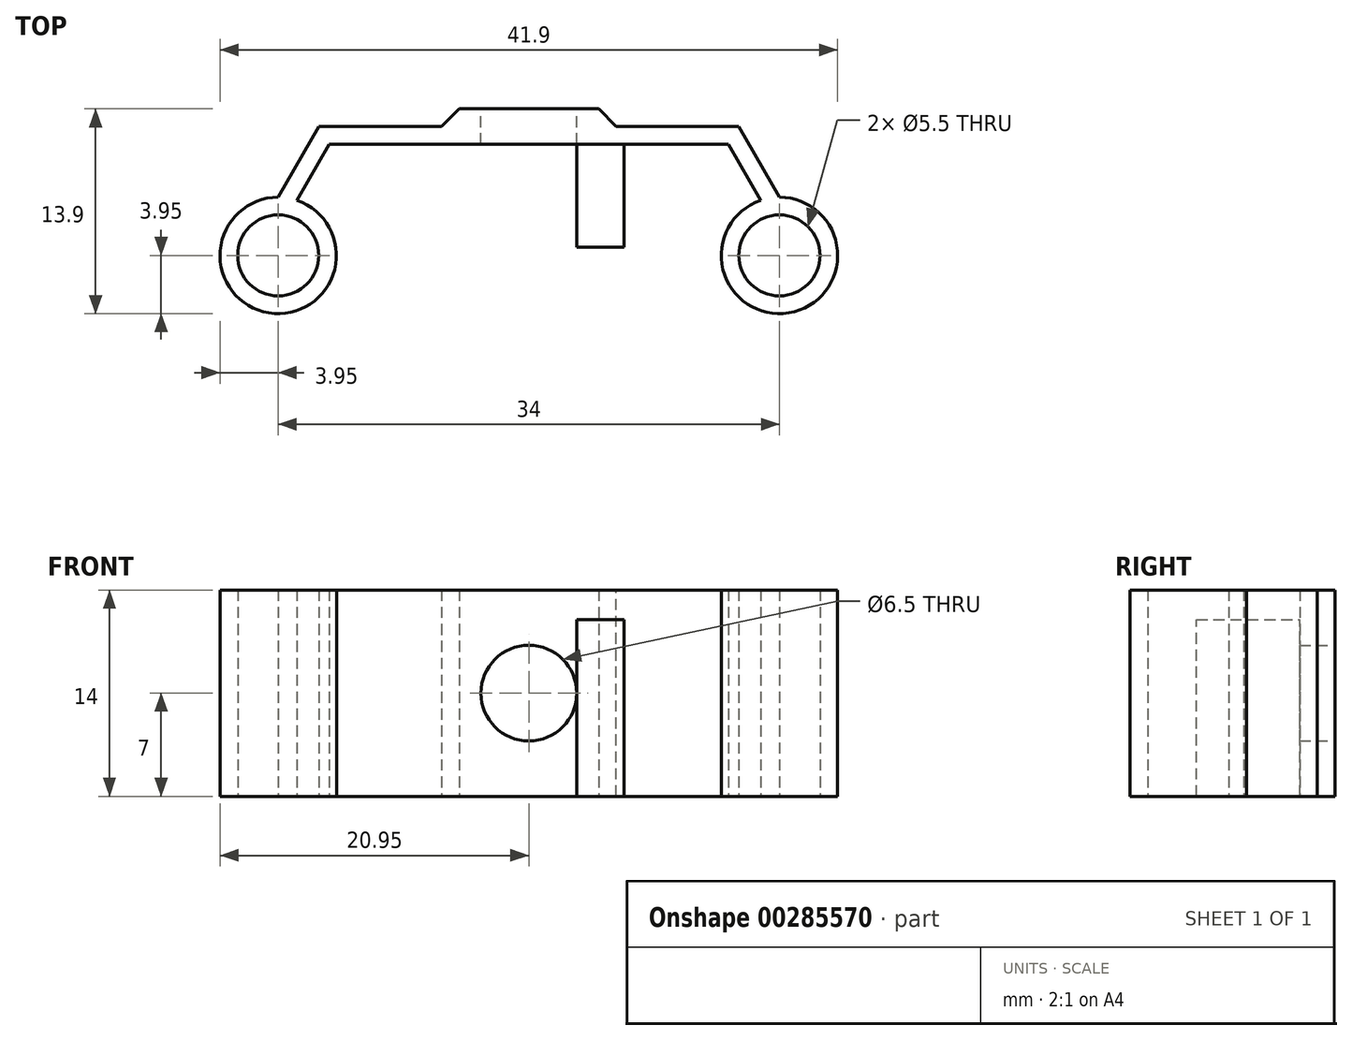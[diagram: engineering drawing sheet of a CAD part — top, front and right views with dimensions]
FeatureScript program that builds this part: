
annotation { "Feature Type Name" : "Feature", "Feature Type Description" : "" }
export const myFeature = defineFeature(function(context is Context, id is Id, definition is map)
    precondition{}
    {
        {
            var Q0;
            Q0=qCreatedBy(makeId("Top.planeOp"),FACE);
            var sketch = newSketch(context, id + "F0", { "sketchPlane" : qUnion([Q0])});
            skCircle(sketch, "E0", {"center": v(0, 0) * mm, "radius": 2.75 * mm});
            skCircle(sketch, "E1.0", {"center": v(0, 0) * mm, "radius": 3.95 * mm});
            skCircle(sketch, "E2", {"center": v(34, 0) * mm, "radius": 2.75 * mm});
            skCircle(sketch, "E3.0", {"center": v(34, 0) * mm, "radius": 3.95 * mm});
            skLineSegment(sketch, "E4", {"start": v(0, 3.95) * mm, "end": v(2.77, 8.75) * mm});
            skLineSegment(sketch, "E5", {"start": v(2.77, 8.75) * mm, "end": v(31.23, 8.75) * mm});
            skLineSegment(sketch, "E6", {"start": v(31.23, 8.75) * mm, "end": v(34, 3.95) * mm});
            skLineSegment(sketch, "E7", {"start": v(1.27, 3.74) * mm, "end": v(3.46, 7.55) * mm});
            skLineSegment(sketch, "E8", {"start": v(3.46, 7.55) * mm, "end": v(30.54, 7.55) * mm});
            skLineSegment(sketch, "E9", {"start": v(30.54, 7.55) * mm, "end": v(32.73, 3.74) * mm});
            skLineSegment(sketch, "E10", {"start": v(12.27, 8.75) * mm, "end": v(12.27, 9.95) * mm});
            skLineSegment(sketch, "E11", {"start": v(12.27, 9.95) * mm, "end": v(21.73, 9.95) * mm});
            skLineSegment(sketch, "E12", {"start": v(21.73, 9.95) * mm, "end": v(21.73, 8.75) * mm});
            skSolve(sketch);
        }
        {
            var Q0;
            Q0=qSketchRegion(id+"F0",true);
            extrude(context, id + "F1", {"entities" : qUnion([Q0]), "depth" : 14 * mm});
        }
        {
            var Q0;
            Q0=makeQuery(id+"F1.opExtrude","SWEPT_FACE",FACE,{"disambiguationData":[OSD([sQuery(id+"F0.wireOp",EDGE,"E5")])]});
            var sketch = newSketch(context, id + "F2", { "sketchPlane" : qUnion([Q0])});
            skCircle(sketch, "E13", {"center": v(-17, 7) * mm, "radius": 3.25 * mm});
            skSolve(sketch);
        }
        {
            var Q0;
            Q0=makeQuery(id+"F2.imprint","IMPRINT",FACE,{"disambiguationData":[TD([[makeQuery(id+"F2.imprint","IMPRINT",EDGE,{"derivedFrom":sQuery(id+"F2.wireOp",EDGE,"E13")}),1.0]])]});
            extrude(context, id + "F3", {"entities" : qUnion([Q0]), "operationType" : NewBodyOperationType.REMOVE, "oppositeDirection" : true, "depth" : 54 * mm});
        }
        {
            var Q0;
            Q0=makeQuery(id+"F3.boolean.opBoolean","COPY",FACE,{"derivedFrom":makeQuery(id+"F3.opExtrude","CAP_FACE",FACE,{"disambiguationData":[OSD([sQuery(id+"F2.wireOp",EDGE,"E13")])],"isStart":true})});
            extrude(context, id + "F4", {"entities" : qUnion([Q0]), "operationType" : NewBodyOperationType.REMOVE, "oppositeDirection" : true, "depth" : 25 * mm});
        }
        {
            var Q0;
            Q0=makeQuery(id+"F1.opExtrude","SWEPT_EDGE",EDGE,{"disambiguationData":[OSD([sQuery(id+"F0.wireOp",EDGE,"E5"),sQuery(id+"F0.wireOp",EDGE,"E12")])]});
            var Q1;
            Q1=makeQuery(id+"F1.opExtrude","SWEPT_EDGE",EDGE,{"disambiguationData":[OSD([sQuery(id+"F0.wireOp",EDGE,"E5"),sQuery(id+"F0.wireOp",EDGE,"E10")])]});
            chamfer(context, id + "F5", {"entities" : qUnion([Q0, Q1]), "width" : 1.2 * mm, "tangentPropagation" : true});
        }
        {
            var Q0;
            Q0=makeQuery(id+"F1.opExtrude","SWEPT_FACE",FACE,{"disambiguationData":[OSD([sQuery(id+"F0.wireOp",EDGE,"E8")])]});
            var sketch = newSketch(context, id + "F6", { "sketchPlane" : qUnion([Q0])});
            skLineSegment(sketch, "E14", {"start": v(23.45, 0) * mm, "end": v(23.45, 12) * mm});
            skLineSegment(sketch, "E15", {"start": v(23.45, 0) * mm, "end": v(20.25, 0) * mm});
            skLineSegment(sketch, "E16", {"start": v(20.25, 0) * mm, "end": v(20.25, 12) * mm});
            skLineSegment(sketch, "E17", {"start": v(20.25, 12) * mm, "end": v(23.45, 12) * mm});
            skSolve(sketch);
        }
        {
            var Q0;
            Q0=makeQuery(id+"F6.imprint","IMPRINT",FACE,{"disambiguationData":[TD([[makeQuery(id+"F6.imprint","IMPRINT",EDGE,{"derivedFrom":sQuery(id+"F6.wireOp",EDGE,"E14")}),1.0]])]});
            extrude(context, id + "F7", {"entities" : qUnion([Q0]), "operationType" : NewBodyOperationType.ADD, "depth" : 7 * mm});
        }
    });
